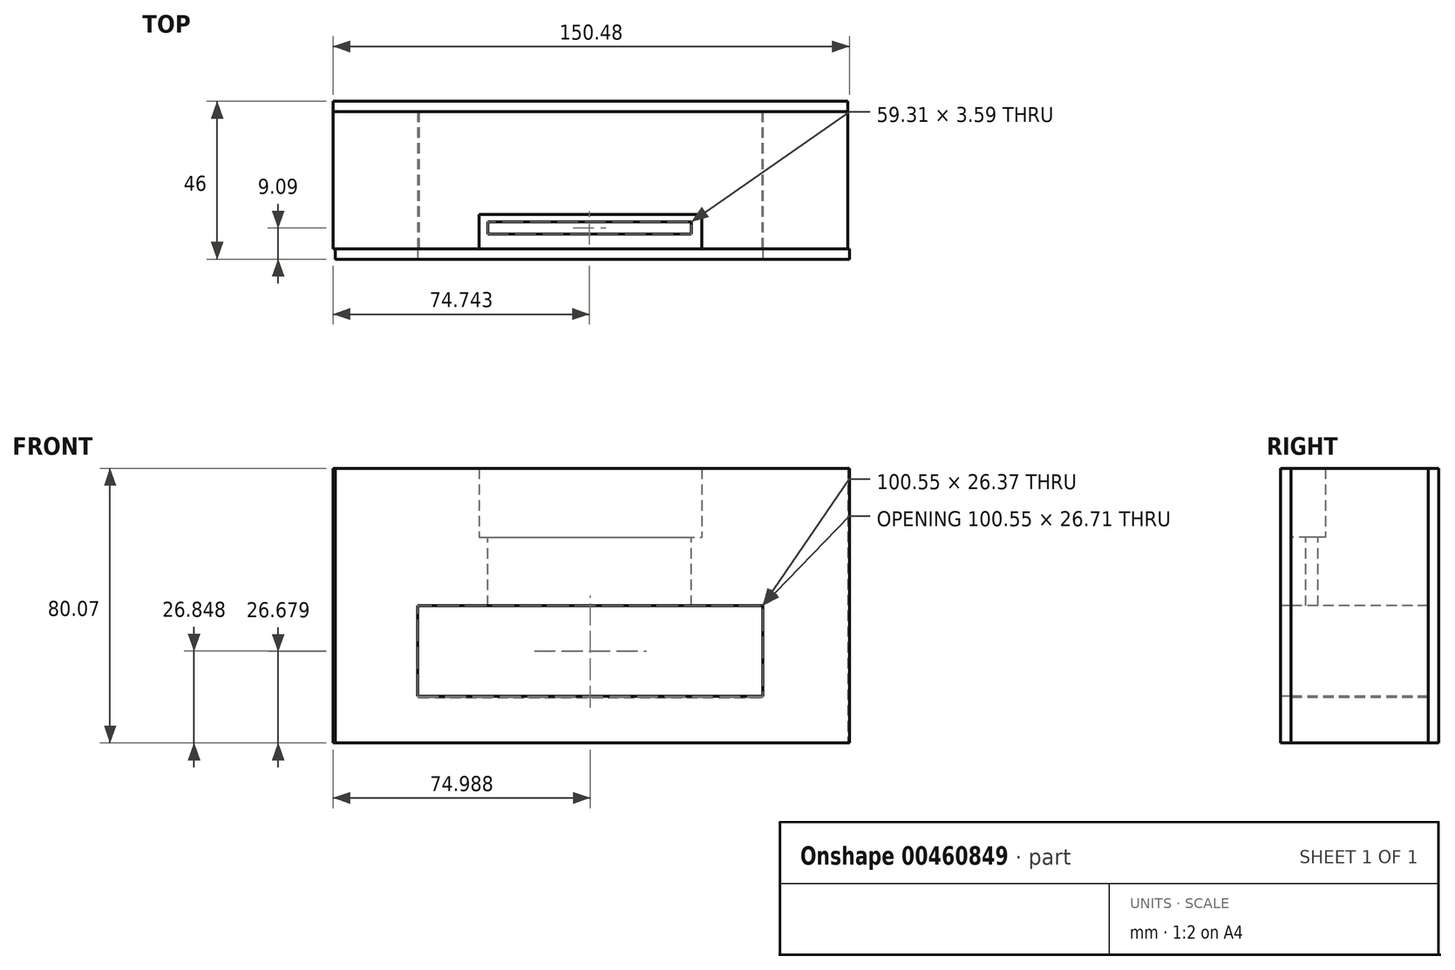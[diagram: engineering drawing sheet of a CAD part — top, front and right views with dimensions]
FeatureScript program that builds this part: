
annotation { "Feature Type Name" : "Feature", "Feature Type Description" : "" }
export const myFeature = defineFeature(function(context is Context, id is Id, definition is map)
    precondition{}
    {
        {
            var Q0;
            Q0=qCreatedBy(makeId("Top.planeOp"),FACE);
            var sketch = newSketch(context, id + "F0", { "sketchPlane" : qUnion([Q0])});
            skLineSegment(sketch, "E0.bottom", {"start": v(75, -20) * mm, "end": v(-75, -20) * mm});
            skLineSegment(sketch, "E0.top", {"start": v(75, 20) * mm, "end": v(-75, 20) * mm});
            skLineSegment(sketch, "E0.left", {"start": v(75, -20) * mm, "end": v(75, 20) * mm});
            skLineSegment(sketch, "E0.right", {"start": v(-75, -20) * mm, "end": v(-75, 20) * mm});
            skPoint(sketch, "E0.middle", {"position": v(0, 0) * mm});
            skSolve(sketch);
        }
        {
            var Q0;
            Q0 = qSketchRegion(id + "F0", true);
            extrude(context, id + "F1", {"entities" : qUnion([Q0]), "depth" : 80 * mm});
        }
        {
            var Q0;
            Q0=makeQuery(id+"F1.opExtrude","SWEPT_FACE",FACE,{"disambiguationData":[OSD([sQuery(id+"F0.wireOp",EDGE,"E0.bottom")])]});
            var sketch = newSketch(context, id + "F2", { "sketchPlane" : qUnion([Q0])});
            skLineSegment(sketch, "E1.bottom", {"start": v(-32.5, 80) * mm, "end": v(32.5, 80) * mm});
            skLineSegment(sketch, "E1.top", {"start": v(-32.5, 60) * mm, "end": v(32.5, 60) * mm});
            skLineSegment(sketch, "E1.left", {"start": v(-32.5, 80) * mm, "end": v(-32.5, 60) * mm});
            skLineSegment(sketch, "E1.right", {"start": v(32.5, 80) * mm, "end": v(32.5, 60) * mm});
            skSolve(sketch);
        }
        {
            var Q0;
            Q0=makeQuery(id+"F2.imprint","IMPRINT",FACE,{"disambiguationData":[TD([[makeQuery(id+"F2.imprint","IMPRINT",EDGE,{"derivedFrom":sQuery(id+"F2.wireOp",EDGE,"E1.top")}),-1.0]])]});
            var sketch = newSketch(context, id + "F3", { "sketchPlane" : qUnion([Q0])});
            skSolve(sketch);
        }
        {
            var Q0;
            Q0 = qSketchRegion(id + "F3", true);
            var Q1;
            Q1=makeQuery(id+"F2.imprint","IMPRINT",FACE,{"disambiguationData":[TD([[makeQuery(id+"F2.imprint","IMPRINT",EDGE,{"derivedFrom":sQuery(id+"F2.wireOp",EDGE,"E1.bottom")}),1.0]])]});
            extrude(context, id + "F4", {"entities" : qUnion([Q0, Q1]), "operationType" : NewBodyOperationType.REMOVE, "oppositeDirection" : true, "depth" : 10 * mm});
        }
        {
            var Q0;
            Q0=makeQuery(id+"F3.imprint","IMPRINT",FACE,{"disambiguationData":[TD([[makeQuery(id+"F3.imprint","IMPRINT",EDGE,{"derivedFrom":makeQuery(id+"F2.imprint","IMPRINT",EDGE,{"derivedFrom":sQuery(id+"F2.wireOp",EDGE,"E1.top")})}),-1.0]])]});
            var sketch = newSketch(context, id + "F5", { "sketchPlane" : qUnion([Q0])});
            skLineSegment(sketch, "E2.bottom", {"start": v(-50, 39.69) * mm, "end": v(50, 39.69) * mm});
            skLineSegment(sketch, "E2.top", {"start": v(-50, 13.32) * mm, "end": v(50, 13.32) * mm});
            skLineSegment(sketch, "E2.left", {"start": v(-50, 39.69) * mm, "end": v(-50, 13.32) * mm});
            skLineSegment(sketch, "E2.right", {"start": v(50, 39.69) * mm, "end": v(50, 13.32) * mm});
            skSolve(sketch);
        }
        {
            var Q0;
            Q0=makeQuery(id+"F3.imprint","IMPRINT",FACE,{"disambiguationData":[TD([[makeQuery(id+"F3.imprint","IMPRINT",EDGE,{"derivedFrom":makeQuery(id+"F2.imprint","IMPRINT",EDGE,{"derivedFrom":sQuery(id+"F2.wireOp",EDGE,"E1.top")})}),-1.0]])]});
            var sketch = newSketch(context, id + "F6", { "sketchPlane" : qUnion([Q0])});
            skLineSegment(sketch, "E3.bottom", {"start": v(-50.06, 39.76) * mm, "end": v(49.71, 39.76) * mm});
            skLineSegment(sketch, "E3.top", {"start": v(-50.06, 12.83) * mm, "end": v(49.71, 12.83) * mm});
            skLineSegment(sketch, "E3.left", {"start": v(-50.06, 39.76) * mm, "end": v(-50.06, 12.83) * mm});
            skLineSegment(sketch, "E3.right", {"start": v(49.71, 39.76) * mm, "end": v(49.71, 12.83) * mm});
            skSolve(sketch);
        }
        {
            var Q0;
            Q0=makeQuery(id+"F5.imprint","IMPRINT",FACE,{"disambiguationData":[TD([[makeQuery(id+"F5.imprint","IMPRINT",EDGE,{"derivedFrom":sQuery(id+"F5.wireOp",EDGE,"E2.bottom")}),-1.0]])]});
            extrude(context, id + "F7", {"entities" : qUnion([Q0]), "operationType" : NewBodyOperationType.REMOVE, "oppositeDirection" : true, "depth" : 53.3 * mm});
        }
        {
            var Q0;
            Q0=makeQuery(id+"F4.boolean.opBoolean","COPY",FACE,{"derivedFrom":makeQuery(id+"F4.opExtrude","SWEPT_FACE",FACE,{"disambiguationData":[OSD([sQuery(id+"F2.wireOp",EDGE,"E1.top")])]})});
            var sketch = newSketch(context, id + "F8", { "sketchPlane" : qUnion([Q0])});
            skLineSegment(sketch, "E4.bottom", {"start": v(-29.91, -12.11) * mm, "end": v(29.4, -12.11) * mm});
            skLineSegment(sketch, "E4.top", {"start": v(-29.91, -15.7) * mm, "end": v(29.4, -15.7) * mm});
            skLineSegment(sketch, "E4.left", {"start": v(-29.91, -12.11) * mm, "end": v(-29.91, -15.7) * mm});
            skLineSegment(sketch, "E4.right", {"start": v(29.4, -12.11) * mm, "end": v(29.4, -15.7) * mm});
            skSolve(sketch);
        }
        {
            var Q0;
            Q0 = qSketchRegion(id + "F8", true);
            extrude(context, id + "F9", {"entities" : qUnion([Q0]), "operationType" : NewBodyOperationType.REMOVE, "oppositeDirection" : true, "depth" : 25 * mm});
        }
        {
            var Q0;
            Q0=makeQuery(id+"F3.imprint","IMPRINT",FACE,{"disambiguationData":[TD([[makeQuery(id+"F3.imprint","IMPRINT",EDGE,{"derivedFrom":makeQuery(id+"F2.imprint","IMPRINT",EDGE,{"derivedFrom":sQuery(id+"F2.wireOp",EDGE,"E1.top")})}),-1.0]])]});
            var sketch = newSketch(context, id + "F10", { "sketchPlane" : qUnion([Q0])});
            skLineSegment(sketch, "E5.bottom", {"start": v(-74.41, 80.07) * mm, "end": v(75.48, 80.07) * mm});
            skLineSegment(sketch, "E5.top", {"start": v(-74.41, 0) * mm, "end": v(75.48, 0) * mm});
            skLineSegment(sketch, "E5.left", {"start": v(-74.41, 80.07) * mm, "end": v(-74.41, 0) * mm});
            skLineSegment(sketch, "E5.right", {"start": v(75.48, 80.07) * mm, "end": v(75.48, 0) * mm});
            skSolve(sketch);
        }
        {
            var Q0;
            Q0 = qSketchRegion(id + "F10", true);
            extrude(context, id + "F11", {"entities" : qUnion([Q0]), "depth" : 3 * mm});
        }
        {
            var Q0;
            Q0=makeQuery(id+"F11.opExtrude","CAP_FACE",FACE,{"disambiguationData":[OSD([sQuery(id+"F10.wireOp",EDGE,"E5.bottom"),sQuery(id+"F10.wireOp",EDGE,"E5.top"),sQuery(id+"F10.wireOp",EDGE,"E5.left"),sQuery(id+"F10.wireOp",EDGE,"E5.right")])],"isStart":false});
            var sketch = newSketch(context, id + "F12", { "sketchPlane" : qUnion([Q0])});
            skPoint(sketch, "E6.firstSnap0", {"position": v(-74.41, 40.03) * mm});
            skLineSegment(sketch, "E6.bottom", {"start": v(-50.29, 40.03) * mm, "end": v(50.26, 40.03) * mm});
            skLineSegment(sketch, "E6.top", {"start": v(-50.29, 13.66) * mm, "end": v(50.26, 13.66) * mm});
            skLineSegment(sketch, "E6.left", {"start": v(-50.29, 40.03) * mm, "end": v(-50.29, 13.66) * mm});
            skLineSegment(sketch, "E6.right", {"start": v(50.26, 40.03) * mm, "end": v(50.26, 13.66) * mm});
            skSolve(sketch);
        }
        {
            var Q0;
            Q0 = qSketchRegion(id + "F12", true);
            extrude(context, id + "F13", {"entities" : qUnion([Q0]), "operationType" : NewBodyOperationType.REMOVE, "oppositeDirection" : true, "depth" : 177.9 * mm});
        }
        {
            var Q0;
            Q0=makeQuery(id+"F1.opExtrude","SWEPT_FACE",FACE,{"disambiguationData":[OSD([sQuery(id+"F0.wireOp",EDGE,"E0.top")])]});
            var sketch = newSketch(context, id + "F14", { "sketchPlane" : qUnion([Q0])});
            skLineSegment(sketch, "E7.bottom", {"start": v(-75, 80) * mm, "end": v(75, 80) * mm});
            skLineSegment(sketch, "E7.top", {"start": v(-75, 0) * mm, "end": v(75, 0) * mm});
            skLineSegment(sketch, "E7.left", {"start": v(-75, 80) * mm, "end": v(-75, 0) * mm});
            skLineSegment(sketch, "E7.right", {"start": v(75, 80) * mm, "end": v(75, 0) * mm});
            skSolve(sketch);
        }
        {
            var Q0;
            Q0 = qSketchRegion(id + "F14", true);
            extrude(context, id + "F15", {"entities" : qUnion([Q0]), "depth" : 3 * mm});
        }
    });
